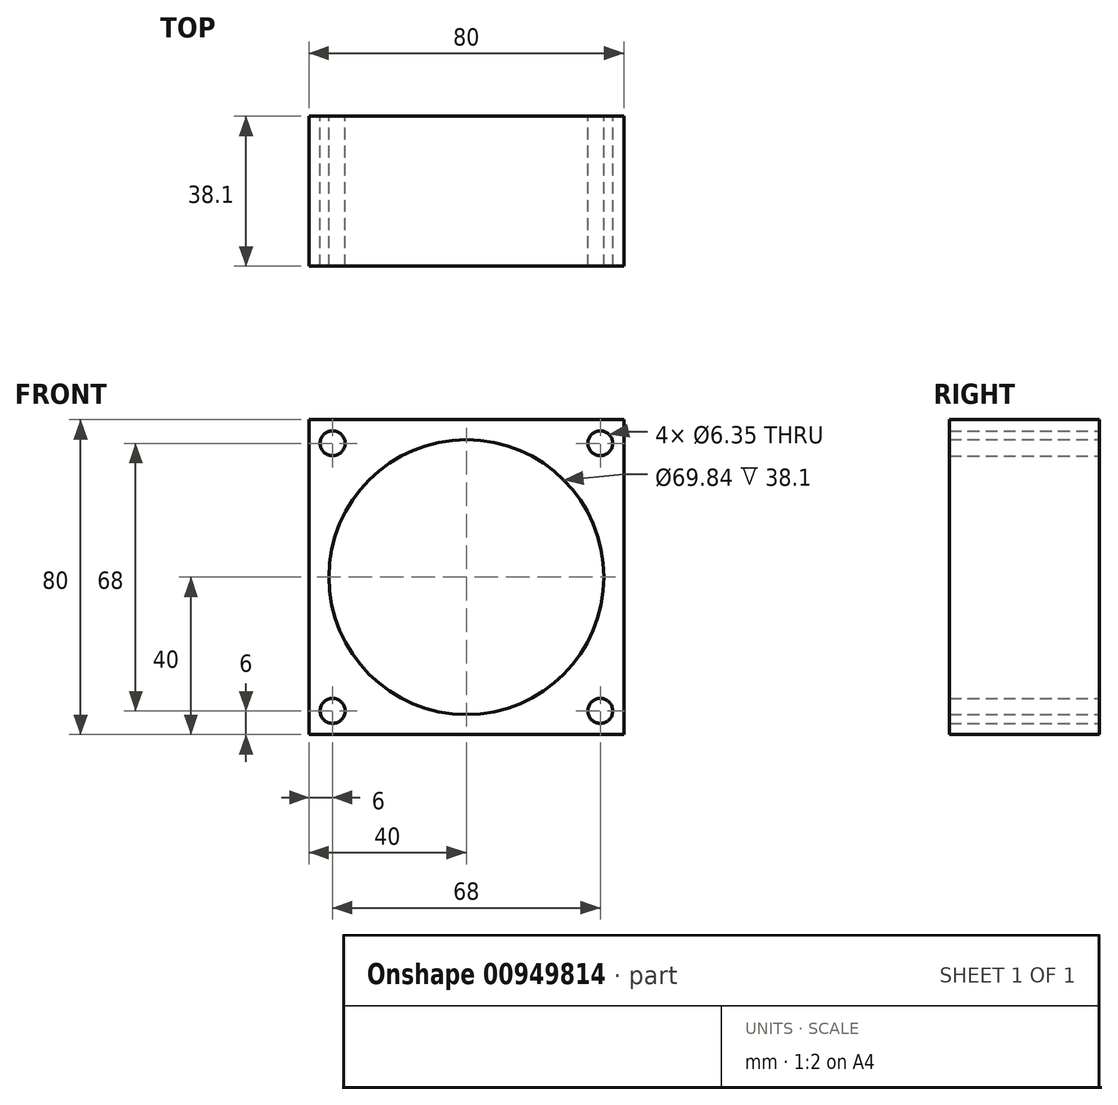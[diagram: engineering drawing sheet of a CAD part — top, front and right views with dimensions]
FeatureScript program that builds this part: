
annotation { "Feature Type Name" : "Feature", "Feature Type Description" : "" }
export const myFeature = defineFeature(function(context is Context, id is Id, definition is map)
    precondition{}
    {
        {
            var Q0;
            Q0=qCreatedBy(makeId("Front.planeOp"),FACE);
            var sketch = newSketch(context, id + "F0", { "sketchPlane" : qUnion([Q0])});
            skLineSegment(sketch, "E0.bottom", {"start": v(40, 40) * mm, "end": v(-40, 40) * mm});
            skLineSegment(sketch, "E0.top", {"start": v(40, -40) * mm, "end": v(-40, -40) * mm});
            skLineSegment(sketch, "E0.left", {"start": v(40, 40) * mm, "end": v(40, -40) * mm});
            skLineSegment(sketch, "E0.right", {"start": v(-40, 40) * mm, "end": v(-40, -40) * mm});
            skPoint(sketch, "E0.middle", {"position": v(0, 0) * mm});
            skLineSegment(sketch, "E1.bottom", {"start": v(-34, 34) * mm, "end": v(34, 34) * mm, "construction": true});
            skLineSegment(sketch, "E1.top", {"start": v(-34, -34) * mm, "end": v(34, -34) * mm, "construction": true});
            skLineSegment(sketch, "E1.left", {"start": v(-34, 34) * mm, "end": v(-34, -34) * mm, "construction": true});
            skLineSegment(sketch, "E1.right", {"start": v(34, 34) * mm, "end": v(34, -34) * mm, "construction": true});
            skCircle(sketch, "E2", {"center": v(34, 34) * mm, "radius": 3.18 * mm});
            skCircle(sketch, "E3", {"center": v(-34, 34) * mm, "radius": 3.18 * mm});
            skCircle(sketch, "E4", {"center": v(-34, -34) * mm, "radius": 3.18 * mm});
            skCircle(sketch, "E5", {"center": v(34, -34) * mm, "radius": 3.18 * mm});
            skCircle(sketch, "E6", {"center": v(0, 0) * mm, "radius": 34.92 * mm});
            skSolve(sketch);
        }
        {
            var Q0;
            Q0=makeQuery(id+"F0.imprint","IMPRINT",FACE,{"disambiguationData":[TD([[makeQuery(id+"F0.imprint","IMPRINT",EDGE,{"derivedFrom":sQuery(id+"F0.wireOp",EDGE,"E0.bottom")}),1.0]])]});
            extrude(context, id + "F1", {"entities" : qUnion([Q0]), "depth" : 38.1 * mm, "offsetDistance" : 25.4 * mm, "symmetric" : true});
        }
    });
